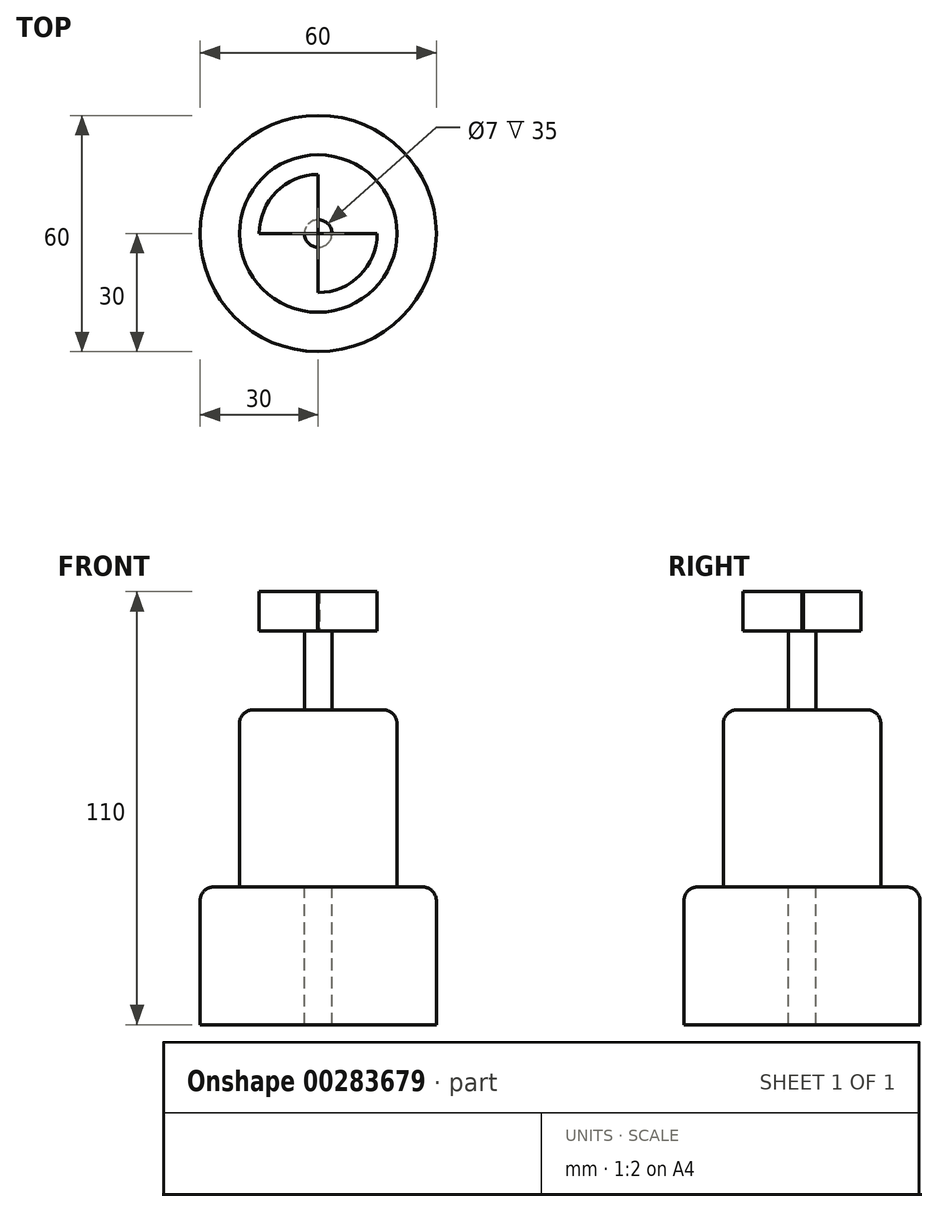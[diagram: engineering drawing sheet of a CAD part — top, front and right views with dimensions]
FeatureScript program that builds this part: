
annotation { "Feature Type Name" : "Feature", "Feature Type Description" : "" }
export const myFeature = defineFeature(function(context is Context, id is Id, definition is map)
    precondition{}
    {
        {
            var Q0;
            Q0=qCreatedBy(makeId("Top.planeOp"),FACE);
            var sketch = newSketch(context, id + "F0", { "sketchPlane" : qUnion([Q0])});
            skCircle(sketch, "E0", {"center": v(0, 0) * mm, "radius": 30 * mm});
            skCircle(sketch, "E1", {"center": v(0, 0) * mm, "radius": 20 * mm});
            skCircle(sketch, "E2", {"center": v(0, 0) * mm, "radius": 3.5 * mm});
            skSolve(sketch);
        }
        {
            var Q0;
            Q0=makeQuery(id+"F0.imprint","IMPRINT",FACE,{"disambiguationData":[TD([[makeQuery(id+"F0.imprint","IMPRINT",EDGE,{"derivedFrom":sQuery(id+"F0.wireOp",EDGE,"E0")}),1.0]])]});
            var Q1;
            Q1=makeQuery(id+"F0.imprint","IMPRINT",FACE,{"disambiguationData":[TD([[makeQuery(id+"F0.imprint","IMPRINT",EDGE,{"derivedFrom":sQuery(id+"F0.wireOp",EDGE,"E1")}),1.0]])]});
            extrude(context, id + "F1", {"entities" : qUnion([Q0, Q1]), "oppositeDirection" : true, "depth" : 35 * mm});
        }
        {
            var Q0;
            Q0=makeQuery(id+"F0.imprint","IMPRINT",FACE,{"disambiguationData":[TD([[makeQuery(id+"F0.imprint","IMPRINT",EDGE,{"derivedFrom":sQuery(id+"F0.wireOp",EDGE,"E1")}),1.0]])]});
            extrude(context, id + "F2", {"entities" : qUnion([Q0]), "operationType" : NewBodyOperationType.ADD, "depth" : 45 * mm});
        }
        {
            var Q0;
            Q0=makeQuery(id+"F0.imprint","IMPRINT",FACE,{"disambiguationData":[TD([[makeQuery(id+"F0.imprint","IMPRINT",EDGE,{"derivedFrom":sQuery(id+"F0.wireOp",EDGE,"E2")}),1.0]])]});
            extrude(context, id + "F3", {"entities" : qUnion([Q0]), "operationType" : NewBodyOperationType.ADD, "depth" : 65 * mm});
        }
        {
            var Q0;
            Q0=qCreatedBy(makeId("Top.planeOp"),FACE);
            cPlane(context, id + "F4", {"entities" : qUnion([Q0]), "cplaneType" : CPlaneType.OFFSET, "offset" : 65 * mm, "width" : 150 * mm, "height" : 150 * mm});
        }
        {
            var Q0;
            Q0=qCreatedBy(id+"F4.planeOp",FACE);
            var sketch = newSketch(context, id + "F5", { "sketchPlane" : qUnion([Q0])});
            skArc(sketch, "E3", {"start": v(0, 15) * mm, "mid": v(-10.6, 10.6) * mm, "end": v(-15, 0) * mm});
            skLineSegment(sketch, "E4", {"start": v(1.84, 0) * mm, "end": v(15, 0) * mm});
            skLineSegment(sketch, "E5", {"start": v(0, -1.84) * mm, "end": v(0, -15) * mm});
            skLineSegment(sketch, "E6", {"start": v(-1.84, 0) * mm, "end": v(-15, 0) * mm});
            skLineSegment(sketch, "E7", {"start": v(0, 3.58) * mm, "end": v(0, 15) * mm});
            skArc(sketch, "E8.trimOffspring", {"start": v(0, -15) * mm, "mid": v(10.6, -10.6) * mm, "end": v(15, 0) * mm});
            skLineSegment(sketch, "E9", {"start": v(-1.84, 0) * mm, "end": v(-0.23, 0) * mm});
            skLineSegment(sketch, "E10", {"start": v(1.84, 0) * mm, "end": v(0.28, 0) * mm});
            skLineSegment(sketch, "E11", {"start": v(0, 0.36) * mm, "end": v(0, 3.58) * mm});
            skLineSegment(sketch, "E12", {"start": v(0, -1.84) * mm, "end": v(0, -0.1) * mm});
            skLineSegment(sketch, "E13", {"start": v(0, 0.36) * mm, "end": v(0.28, 0) * mm});
            skLineSegment(sketch, "E14", {"start": v(0, -0.1) * mm, "end": v(-0.23, 0) * mm});
            skSolve(sketch);
        }
        {
            var Q0;
            Q0=makeQuery(id+"F5.imprint","IMPRINT",FACE,{"disambiguationData":[TD([[makeQuery(id+"F5.imprint","IMPRINT",EDGE,{"derivedFrom":sQuery(id+"F5.wireOp",EDGE,"E3")}),1.0]])]});
            extrude(context, id + "F6", {"entities" : qUnion([Q0]), "operationType" : NewBodyOperationType.ADD, "depth" : 10 * mm});
        }
        {
            var Q0;
            Q0=makeQuery(id+"F2.opExtrude","CAP_EDGE",EDGE,{"disambiguationData":[OSD([sQuery(id+"F0.wireOp",EDGE,"E1")])],"isStart":false});
            var Q1;
            Q1=makeQuery(id+"F1.opExtrude","CAP_EDGE",EDGE,{"disambiguationData":[OSD([sQuery(id+"F0.wireOp",EDGE,"E0")])],"isStart":true});
            fillet(context, id + "F7", {"entities" : qUnion([Q0, Q1]), "radius" : 3.5 * mm, "tangentPropagation" : true, "allowEdgeOverflow" : false});
        }
    });
